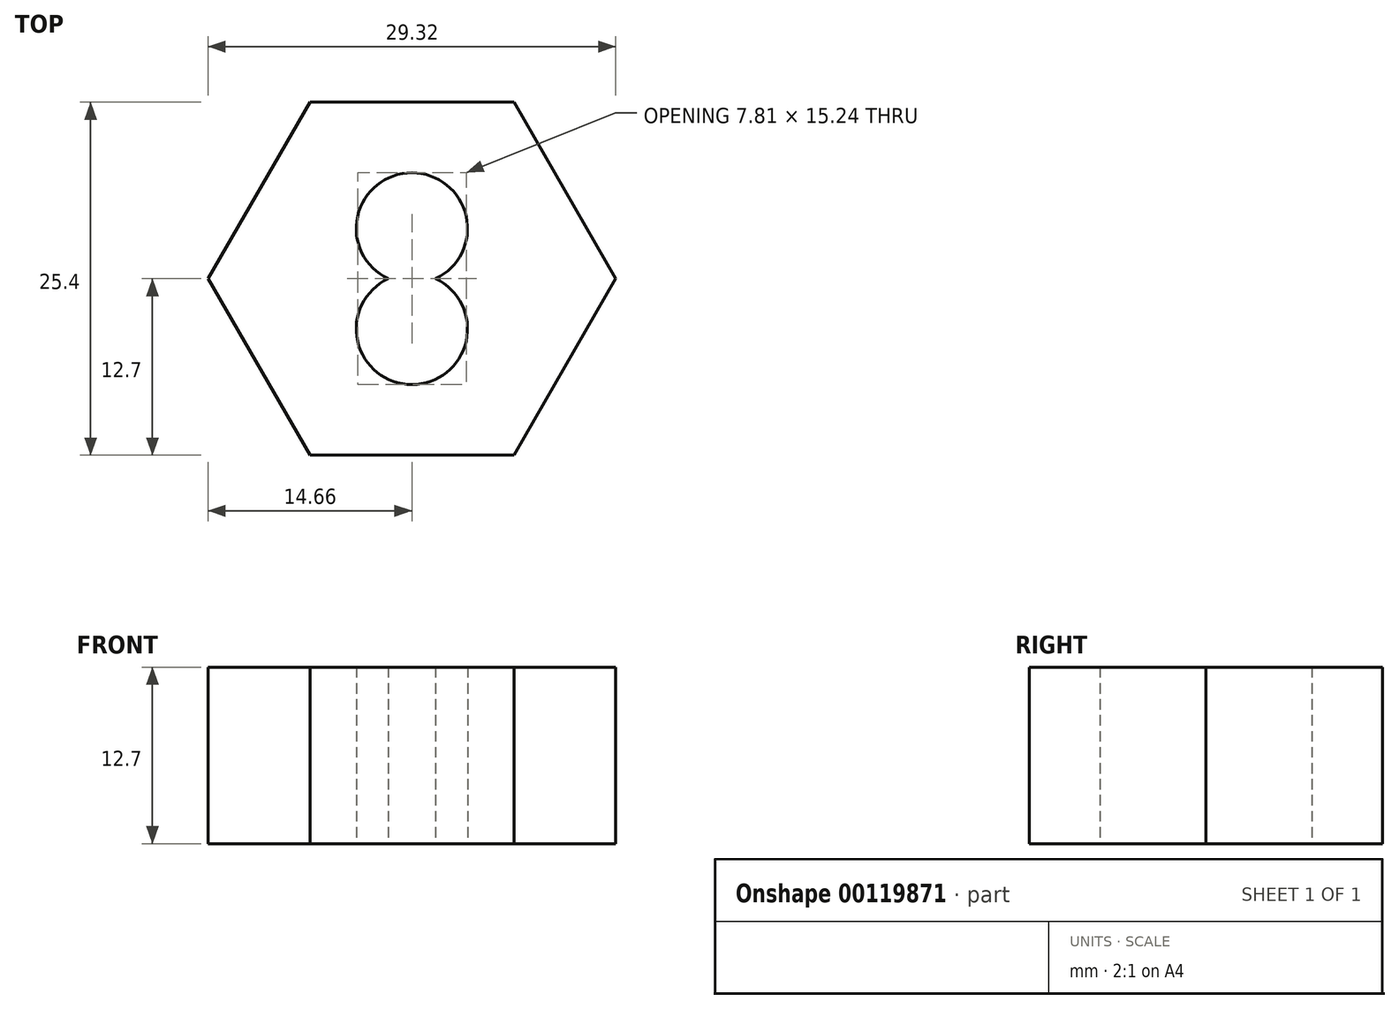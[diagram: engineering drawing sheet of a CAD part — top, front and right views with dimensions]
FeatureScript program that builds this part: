
annotation { "Feature Type Name" : "Feature", "Feature Type Description" : "" }
export const myFeature = defineFeature(function(context is Context, id is Id, definition is map)
    precondition{}
    {
        {
            var Q0;
            Q0=qCreatedBy(makeId("Top.planeOp"),FACE);
            var sketch = newSketch(context, id + "F3", { "sketchPlane" : qUnion([Q0])});
            skCircle(sketch, "E0", {"center": v(0, 0) * mm, "radius": 4 * mm});
            skCircle(sketch, "E1", {"center": v(0, -3.62) * mm, "radius": 12.7 * mm});
            skCircle(sketch, "E2", {"center": v(0, -7.24) * mm, "radius": 4 * mm});
            skLineSegment(sketch, "E3", {"start": v(0, -7.24) * mm, "end": v(0, 0) * mm});
            skSolve(sketch);
        }
        {
            var Q0;
            Q0=makeQuery(id+"F3.imprint","IMPRINT",FACE,{"disambiguationData":[TD([[makeQuery(id+"F3.imprint","IMPRINT",EDGE,{"derivedFrom":sQuery(id+"F3.wireOp",EDGE,"E1")}),1.0]])]});
            extrude(context, id + "F0", {"entities" : qUnion([Q0]), "depth" : 12.7 * mm});
        }
        {
            var Q0;
            Q0=makeQuery(id+"F0.opExtrude","CAP_FACE",FACE,{"disambiguationData":[OSD([sQuery(id+"F3.wireOp",EDGE,"E0"),sQuery(id+"F3.wireOp",EDGE,"E1"),sQuery(id+"F3.wireOp",EDGE,"E2")])],"isStart":false});
            var sketch = newSketch(context, id + "F1", { "sketchPlane" : qUnion([Q0])});
            skCircle(sketch, "E4.0", {"center": v(0, -3.62) * mm, "radius": 12.7 * mm, "construction": true});
            skLineSegment(sketch, "E5.0", {"start": v(7.33, -16.32) * mm, "end": v(-7.33, -16.32) * mm});
            skLineSegment(sketch, "E5.1", {"start": v(-7.33, -16.32) * mm, "end": v(-14.66, -3.62) * mm});
            skLineSegment(sketch, "E5.2", {"start": v(-14.66, -3.62) * mm, "end": v(-7.33, 9.08) * mm});
            skLineSegment(sketch, "E5.3", {"start": v(-7.33, 9.08) * mm, "end": v(7.33, 9.08) * mm});
            skLineSegment(sketch, "E5.4", {"start": v(7.33, 9.08) * mm, "end": v(14.66, -3.62) * mm});
            skLineSegment(sketch, "E5.5", {"start": v(14.66, -3.62) * mm, "end": v(7.33, -16.32) * mm});
            skPoint(sketch, "E5.0.midPoint", {"position": v(0, -16.32) * mm});
            skSolve(sketch);
        }
        {
            var Q0;
            {var subQ0=sQuery(id+"F1.wireOp",EDGE,"E5.5");var subQ1=sQuery(id+"F1.wireOp",EDGE,"E5.4");var subQ2=makeQuery(id+"F1.imprint","INTERSECT",VERTEX,{"derivedFrom":[subQ1,subQ0]});Q0=makeQuery(id+"F1.imprint","IMPRINT",FACE,{"disambiguationData":[TD([[makeQuery(id+"F1.imprint","IMPRINT",EDGE,{"disambiguationData":[TD([[subQ2,1.0]])],"derivedFrom":subQ1}),-1.0]])]});}
            var Q1;
            {var subQ0=sQuery(id+"F1.wireOp",EDGE,"E5.2");var subQ1=sQuery(id+"F1.wireOp",EDGE,"E5.1");var subQ2=makeQuery(id+"F1.imprint","INTERSECT",VERTEX,{"derivedFrom":[subQ1,subQ0]});Q1=makeQuery(id+"F1.imprint","IMPRINT",FACE,{"disambiguationData":[TD([[makeQuery(id+"F1.imprint","IMPRINT",EDGE,{"disambiguationData":[TD([[subQ2,1.0]])],"derivedFrom":subQ1}),-1.0]])]});}
            var Q2;
            {var subQ0=sQuery(id+"F1.wireOp",EDGE,"E5.3");var subQ1=sQuery(id+"F1.wireOp",EDGE,"E5.2");var subQ2=makeQuery(id+"F1.imprint","INTERSECT",VERTEX,{"derivedFrom":[subQ1,subQ0]});Q2=makeQuery(id+"F1.imprint","IMPRINT",FACE,{"disambiguationData":[TD([[makeQuery(id+"F1.imprint","IMPRINT",EDGE,{"disambiguationData":[TD([[subQ2,1.0]])],"derivedFrom":subQ1}),-1.0]])]});}
            var Q3;
            {var subQ0=sQuery(id+"F1.wireOp",EDGE,"E5.4");var subQ1=sQuery(id+"F1.wireOp",EDGE,"E5.3");var subQ2=makeQuery(id+"F1.imprint","INTERSECT",VERTEX,{"derivedFrom":[subQ1,subQ0]});Q3=makeQuery(id+"F1.imprint","IMPRINT",FACE,{"disambiguationData":[TD([[makeQuery(id+"F1.imprint","IMPRINT",EDGE,{"disambiguationData":[TD([[subQ2,1.0]])],"derivedFrom":subQ1}),-1.0]])]});}
            var Q4;
            {var subQ0=sQuery(id+"F1.wireOp",EDGE,"E5.5");var subQ1=sQuery(id+"F1.wireOp",EDGE,"E5.0");var subQ2=makeQuery(id+"F1.imprint","INTERSECT",VERTEX,{"derivedFrom":[subQ1,subQ0]});Q4=makeQuery(id+"F1.imprint","IMPRINT",FACE,{"disambiguationData":[TD([[makeQuery(id+"F1.imprint","IMPRINT",EDGE,{"disambiguationData":[TD([[subQ2,-1.0]])],"derivedFrom":subQ1}),-1.0]])]});}
            var Q5;
            {var subQ0=sQuery(id+"F1.wireOp",EDGE,"E5.1");var subQ1=sQuery(id+"F1.wireOp",EDGE,"E5.0");var subQ2=makeQuery(id+"F1.imprint","INTERSECT",VERTEX,{"derivedFrom":[subQ1,subQ0]});Q5=makeQuery(id+"F1.imprint","IMPRINT",FACE,{"disambiguationData":[TD([[makeQuery(id+"F1.imprint","IMPRINT",EDGE,{"disambiguationData":[TD([[subQ2,1.0]])],"derivedFrom":subQ1}),-1.0]])]});}
            extrude(context, id + "F2", {"entities" : qUnion([Q0, Q1, Q2, Q3, Q4, Q5]), "operationType" : NewBodyOperationType.ADD, "oppositeDirection" : true, "depth" : 12.7 * mm});
        }
    });
